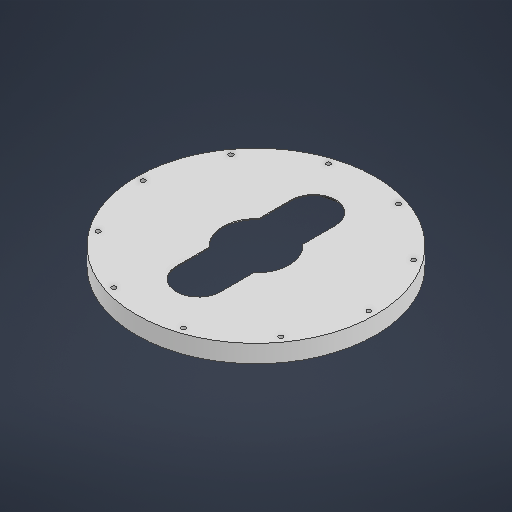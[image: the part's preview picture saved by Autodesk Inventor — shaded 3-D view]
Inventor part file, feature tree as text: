
AUTODESK INVENTOR PART (.ipt)
format: ipt  version: 2025 (Build 290162000, 162)  size: 283,648 bytes
history: native  units: in
note: dims shown in document units (in); Inventor stores cm internally (conversion verified against a paired STEP export)
features: sketch x9, extrude x7, hole x1
ambient origin geometry x8: Origin, YZ Plane, XZ Plane, XY Plane, X Axis, Y Axis, Z Axis, Center Point
bodies: Solid1 (feature_tree)
feature tree (17):
  extrude  "Extrusion1"  Depth=8.6614in
  extrude  "Extrusion2"  Depth=2.1654in
  extrude  "Extrusion3"  TaperAngle=0.0deg  [1 undecoded]
  extrude  "Extrusion4"  Depth=0.7874in
  hole  "Hole1"  [1 undecoded]
  extrude  "Extrusion5"  Depth=10.0394in
  extrude  "Extrusion6"  Depth=3.937in TaperAngle=360.0deg
  extrude  "Extrusion7"  Depth=0.3937in TaperAngle=0.0deg
  sketch  "Sketch1"  dims[d0=10.6299in d1=8.6614in]
  sketch  "Sketch2"  dims[d5=0.1969in d6=0.0in d7=0.0in]
  sketch  "Sketch3"  dims[d8=0.7874in d9=0.0in d10=2.7559in]
  sketch  "Sketch4"  dims[d11=0.7874in d12=7.874in]
  sketch  "Sketch5"  dims[d13=0.0in d14=0.0in d15=10.0394in]
  sketch  "Sketch Circular Pattern1"  dims[d2=2.1654in d3=0.0in d4=1.4173in]
  sketch  "Sketch6"  dims[d16=0.1575in d17=3.937in d19=360.0deg]
  sketch  "Sketch7"  dims[d21=0.1969in d22=0.3937in d23=0.4094in d24=0.0787in d25=90.0deg d26=0.315in d27=0.8108in d28=0.5906in d29=0.0in]
  sketch  "Sketch8"  dims[d30=2.9528in d33=0.0394in d34=0.0in d38=0.5512in d39=0.0in d40=0.0197in d41=0.0344in d42=0.0197in d43=0.0344in]
note: 2 required parameter values undecoded (feature->parameter linkage not recoverable at this tier; creation-order binding heuristic only, values carry confidence <= 0.55)
